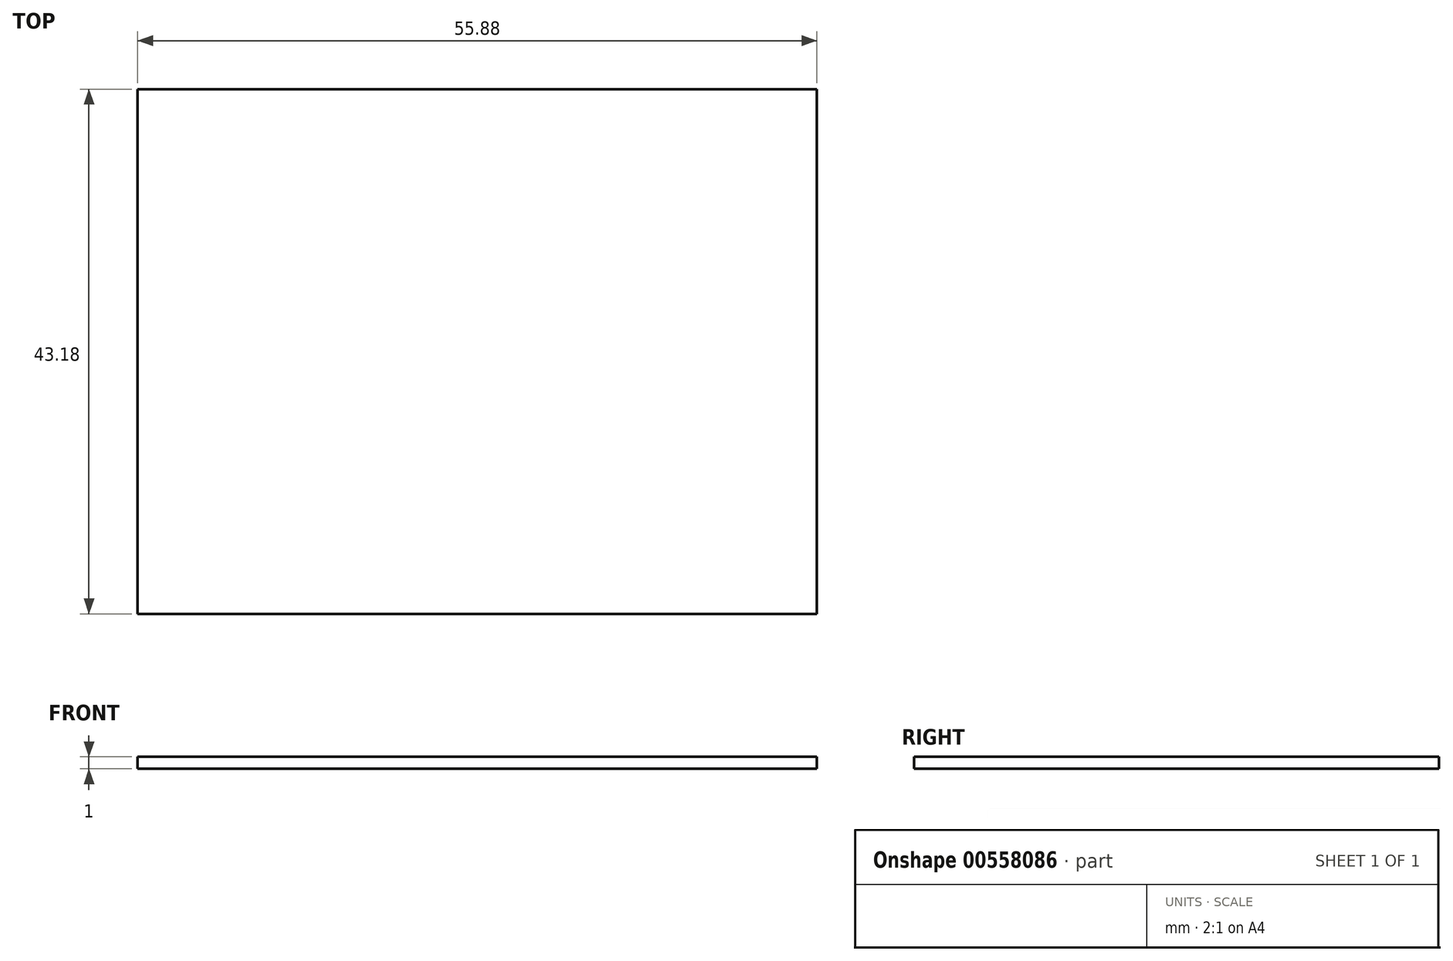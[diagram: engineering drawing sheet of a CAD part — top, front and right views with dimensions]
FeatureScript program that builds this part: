
annotation { "Feature Type Name" : "Feature", "Feature Type Description" : "" }
export const myFeature = defineFeature(function(context is Context, id is Id, definition is map)
    precondition{}
    {
        {
            var Q0;
            Q0=qCreatedBy(makeId("Top.planeOp"),FACE);
            var sketch = newSketch(context, id + "F0", { "sketchPlane" : qUnion([Q0])});
            skLineSegment(sketch, "E0.bottom", {"start": v(-27.85, 22.42) * mm, "end": v(28.03, 22.42) * mm});
            skLineSegment(sketch, "E0.top", {"start": v(-27.85, -20.76) * mm, "end": v(28.03, -20.76) * mm});
            skLineSegment(sketch, "E0.left", {"start": v(-27.85, 22.42) * mm, "end": v(-27.85, -20.76) * mm});
            skLineSegment(sketch, "E0.right", {"start": v(28.03, 22.42) * mm, "end": v(28.03, -20.76) * mm});
            skSolve(sketch);
        }
        {
            var Q0;
            Q0=makeQuery(id+"F0.imprint","IMPRINT",FACE,{"disambiguationData":[TD([[makeQuery(id+"F0.imprint","IMPRINT",EDGE,{"derivedFrom":sQuery(id+"F0.wireOp",EDGE,"E0.bottom")}),-1.0]])]});
            extrude(context, id + "F1", {"entities" : qUnion([Q0]), "depth" : 1 * mm, "offsetDistance" : 25 * mm});
        }
    });
